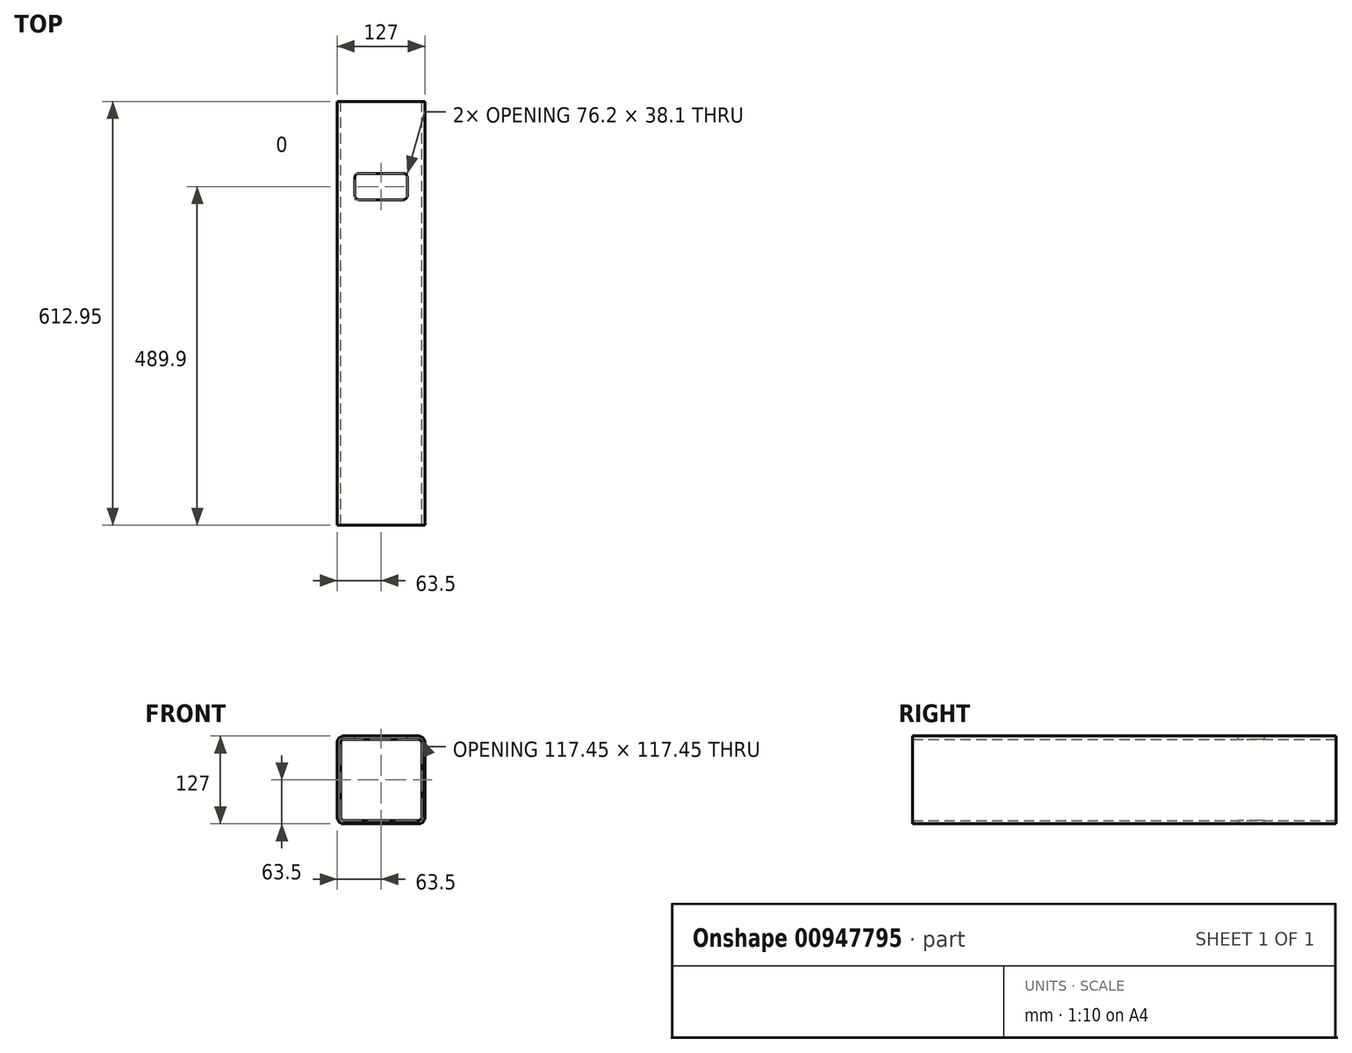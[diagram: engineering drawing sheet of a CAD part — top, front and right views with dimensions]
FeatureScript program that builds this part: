
annotation { "Feature Type Name" : "Feature", "Feature Type Description" : "" }
export const myFeature = defineFeature(function(context is Context, id is Id, definition is map)
    precondition{}
    {
        {
            var Q0;
            Q0=qCreatedBy(makeId("Front.planeOp"),FACE);
            var sketch = newSketch(context, id + "F0", { "sketchPlane" : qUnion([Q0])});
            skLineSegment(sketch, "E0.bottom", {"start": v(53.95, -63.5) * mm, "end": v(-53.95, -63.5) * mm});
            skLineSegment(sketch, "E0.top", {"start": v(53.95, 63.5) * mm, "end": v(-53.95, 63.5) * mm});
            skLineSegment(sketch, "E0.left", {"start": v(63.5, -53.95) * mm, "end": v(63.5, 53.95) * mm});
            skLineSegment(sketch, "E0.right", {"start": v(-63.5, -53.95) * mm, "end": v(-63.5, 53.95) * mm});
            skPoint(sketch, "E0.middle", {"position": v(0, 0) * mm});
            skLineSegment(sketch, "E1.bottom", {"start": v(53.95, -58.73) * mm, "end": v(-53.95, -58.73) * mm});
            skLineSegment(sketch, "E1.top", {"start": v(53.95, 58.73) * mm, "end": v(-53.95, 58.73) * mm});
            skLineSegment(sketch, "E1.left", {"start": v(58.73, -53.95) * mm, "end": v(58.73, 53.95) * mm});
            skLineSegment(sketch, "E1.right", {"start": v(-58.73, -53.95) * mm, "end": v(-58.73, 53.95) * mm});
            skPoint(sketch, "E2.visualSharp", {"position": v(-58.73, 58.73) * mm});
            skArc(sketch, "E2.filletArc", {"start": v(-53.95, 58.73) * mm, "mid": v(-57.33, 57.33) * mm, "end": v(-58.73, 53.95) * mm});
            skPoint(sketch, "E3.visualSharp", {"position": v(58.73, 58.73) * mm});
            skArc(sketch, "E3.filletArc", {"start": v(58.73, 53.95) * mm, "mid": v(57.33, 57.33) * mm, "end": v(53.95, 58.73) * mm});
            skPoint(sketch, "E4.visualSharp", {"position": v(58.73, -58.73) * mm});
            skArc(sketch, "E4.filletArc", {"start": v(53.95, -58.73) * mm, "mid": v(57.33, -57.33) * mm, "end": v(58.73, -53.95) * mm});
            skPoint(sketch, "E5.visualSharp", {"position": v(-58.73, -58.73) * mm});
            skArc(sketch, "E5.filletArc", {"start": v(-58.73, -53.95) * mm, "mid": v(-57.33, -57.33) * mm, "end": v(-53.95, -58.73) * mm});
            skPoint(sketch, "E6.visualSharp", {"position": v(-63.5, 63.5) * mm});
            skArc(sketch, "E6.filletArc", {"start": v(-53.95, 63.5) * mm, "mid": v(-60.7, 60.7) * mm, "end": v(-63.5, 53.95) * mm});
            skPoint(sketch, "E7.visualSharp", {"position": v(63.5, 63.5) * mm});
            skArc(sketch, "E7.filletArc", {"start": v(63.5, 53.95) * mm, "mid": v(60.7, 60.7) * mm, "end": v(53.95, 63.5) * mm});
            skPoint(sketch, "E8.visualSharp", {"position": v(63.5, -63.5) * mm});
            skArc(sketch, "E8.filletArc", {"start": v(53.95, -63.5) * mm, "mid": v(60.7, -60.7) * mm, "end": v(63.5, -53.95) * mm});
            skPoint(sketch, "E9.visualSharp", {"position": v(-63.5, -63.5) * mm});
            skArc(sketch, "E9.filletArc", {"start": v(-63.5, -53.95) * mm, "mid": v(-60.7, -60.7) * mm, "end": v(-53.95, -63.5) * mm});
            skSolve(sketch);
        }
        {
            var Q0;
            Q0 = qSketchRegion(id + "F0", true);
            extrude(context, id + "F1", {"entities" : qUnion([Q0]), "depth" : 612.95 * mm, "offsetDistance" : 25 * mm});
        }
        {
            var Q0;
            Q0=makeQuery(id+"F1.opExtrude","SWEPT_FACE",FACE,{"disambiguationData":[OSD([sQuery(id+"F0.wireOp",EDGE,"E0.top")])]});
            var sketch = newSketch(context, id + "F2", { "sketchPlane" : qUnion([Q0])});
            skLineSegment(sketch, "E10.bottom", {"start": v(31.75, -142.1) * mm, "end": v(-31.75, -142.1) * mm});
            skLineSegment(sketch, "E10.top", {"start": v(31.75, -104) * mm, "end": v(-31.75, -104) * mm});
            skLineSegment(sketch, "E10.left", {"start": v(38.1, -135.75) * mm, "end": v(38.1, -110.35) * mm});
            skLineSegment(sketch, "E10.right", {"start": v(-38.1, -135.75) * mm, "end": v(-38.1, -110.35) * mm});
            skPoint(sketch, "E10.middle", {"position": v(0, -123.05) * mm});
            skPoint(sketch, "E11.visualSharp", {"position": v(-38.1, -104) * mm});
            skArc(sketch, "E11.filletArc", {"start": v(-31.75, -104) * mm, "mid": v(-36.24, -105.86) * mm, "end": v(-38.1, -110.35) * mm});
            skPoint(sketch, "E12.visualSharp", {"position": v(38.1, -104) * mm});
            skArc(sketch, "E12.filletArc", {"start": v(38.1, -110.35) * mm, "mid": v(36.24, -105.86) * mm, "end": v(31.75, -104) * mm});
            skPoint(sketch, "E13.visualSharp", {"position": v(38.1, -142.1) * mm});
            skArc(sketch, "E13.filletArc", {"start": v(31.75, -142.1) * mm, "mid": v(36.24, -140.24) * mm, "end": v(38.1, -135.75) * mm});
            skPoint(sketch, "E14.visualSharp", {"position": v(-38.1, -142.1) * mm});
            skArc(sketch, "E14.filletArc", {"start": v(-38.1, -135.75) * mm, "mid": v(-36.24, -140.24) * mm, "end": v(-31.75, -142.1) * mm});
            skSolve(sketch);
        }
        {
            var Q0;
            Q0 = qSketchRegion(id + "F2", true);
            extrude(context, id + "F3", {"entities" : qUnion([Q0]), "operationType" : NewBodyOperationType.REMOVE, "endBound" : BoundingType.THROUGH_ALL, "oppositeDirection" : true, "depth" : 25 * mm, "offsetDistance" : 25 * mm});
        }
    });
